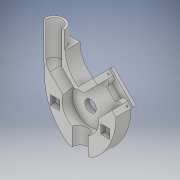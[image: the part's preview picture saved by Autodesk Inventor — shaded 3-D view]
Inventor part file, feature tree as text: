
AUTODESK INVENTOR PART (.ipt)
format: ipt  version: 2019 (Build 230136000, 136)  size: 598,016 bytes
history: native  units: mm
features: sketch x21, extrude x17, projected_geometry x3, sweep x2, other x2, fillet x2
ambient origin geometry x8: Origin, YZ Plane, XZ Plane, XY Plane, X Axis, Y Axis, Z Axis, Center Point
bodies: Body1 (feature_tree)
feature tree (47):
  extrude  "Extrusion2"  Depth=80.0mm
  sketch  "Esquisse3"
  sweep  "Balayage1"
  extrude  "Extrusion6"  Depth=32.0mm
  extrude  "Extrusion7"  Depth=18.0mm TaperAngle=0.0deg
  extrude  "Extrusion8"  TaperAngle=135.0deg  [1 undecoded]
  sketch  "Esquisse11"
  sketch  "Esquisse12"
  other  "Plan de construction1"
  sketch  "Esquisse13"
  extrude  "Extrusion9"  Depth=23.0mm
  extrude  "Extrusion10"  Depth=14.0mm
  other  "Plan de construction2"
  sketch  "Esquisse14"
  extrude  "Extrusion11"  Depth=4.0mm
  extrude  "Extrusion12"  TaperAngle=0.0deg  [1 undecoded]
  extrude  "Extrusion13"  Depth=4.0mm TaperAngle=0.0deg
  extrude  "Extrusion14"  Depth=10.0mm
  extrude  "Extrusion15"  Depth=4.0mm TaperAngle=0.0deg
  sketch  "Esquisse20"
  sketch  "Esquisse21"
  sketch  "Esquisse24"
  extrude  "Extrusion17"  Depth=2.0mm
  sweep  "Balayage4"
  extrude  "Extrusion18"  Depth=35.0mm
  extrude  "Extrusion19"  Depth=17.5mm
  extrude  "Extrusion20"  Depth=8.5mm
  extrude  "Extrusion21"  Depth=12.0mm TaperAngle=0.0deg
  fillet  "Congé1"  Radius=30.0mm
  extrude  "Extrusion22"  Depth=28.0mm
  fillet  "Congé2"  Radius=17.0mm
  sketch  "Esquisse2"
  sketch  "Esquisse4"
  sketch  "Esquisse8"
  sketch  "Esquisse9"
  sketch  "Esquisse10"
  sketch  "Esquisse16"
  projected_geometry  "Boucle projetée3"
  sketch  "Esquisse18"
  sketch  "Esquisse19"
  projected_geometry  "Boucle projetée4"
  projected_geometry  "Boucle projetée6"
  sketch  "Esquisse25"
  sketch  "Esquisse26"
  sketch  "Esquisse27"
  sketch  "Esquisse28"
  sketch  "Esquisse29"
note: 2 required parameter values undecoded (feature->parameter linkage not recoverable at this tier; creation-order binding heuristic only, values carry confidence <= 0.55)
